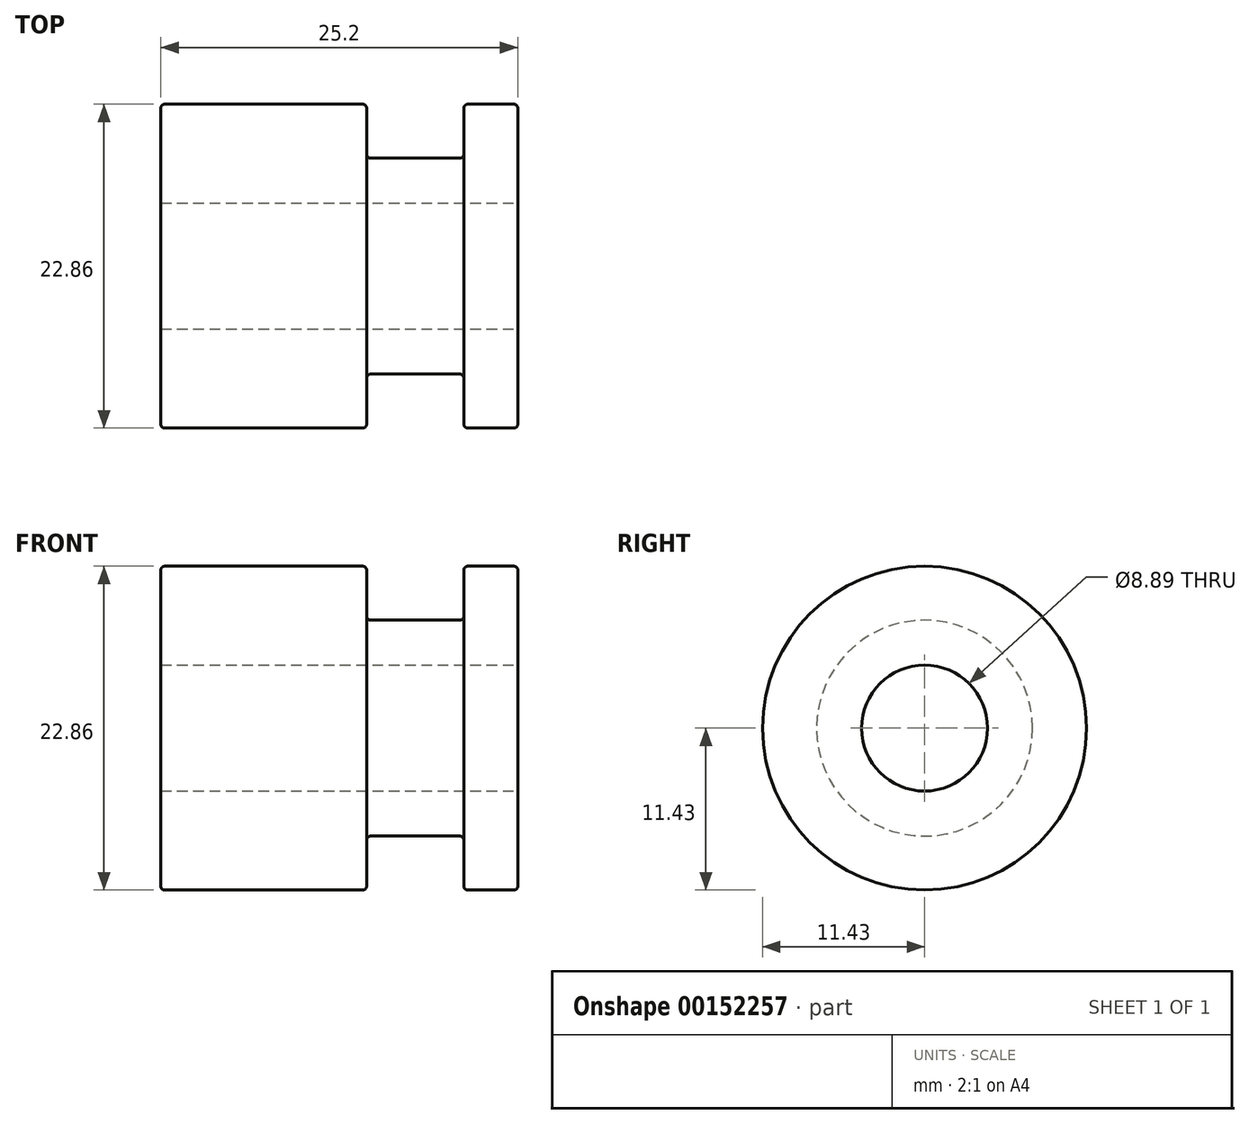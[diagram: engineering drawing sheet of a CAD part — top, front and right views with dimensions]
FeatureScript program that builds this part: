
annotation { "Feature Type Name" : "Feature", "Feature Type Description" : "" }
export const myFeature = defineFeature(function(context is Context, id is Id, definition is map)
    precondition{}
    {
        {
            var Q0;
            Q0=qCreatedBy(makeId("Front.planeOp"),FACE);
            var sketch = newSketch(context, id + "F0", { "sketchPlane" : qUnion([Q0])});
            skLineSegment(sketch, "E0", {"start": v(0, 0) * mm, "end": v(0, 11.15) * mm});
            skLineSegment(sketch, "E1", {"start": v(-0.28, 11.43) * mm, "end": v(-3.53, 11.43) * mm});
            skLineSegment(sketch, "E2", {"start": v(-3.8, 11.15) * mm, "end": v(-3.8, 7.9) * mm});
            skLineSegment(sketch, "E3", {"start": v(-4.1, 7.62) * mm, "end": v(-10.39, 7.62) * mm});
            skLineSegment(sketch, "E4", {"start": v(-10.67, 7.9) * mm, "end": v(-10.67, 11.15) * mm});
            skLineSegment(sketch, "E5", {"start": v(-10.95, 11.43) * mm, "end": v(-24.92, 11.43) * mm});
            skLineSegment(sketch, "E6", {"start": v(-25.2, 11.15) * mm, "end": v(-25.2, 7.62) * mm});
            skLineSegment(sketch, "E7", {"start": v(-25.2, 7.62) * mm, "end": v(-25.2, 0) * mm});
            skLineSegment(sketch, "E8", {"start": v(-25.2, 0) * mm, "end": v(0, 0) * mm});
            skPoint(sketch, "E9.visualSharp", {"position": v(-3.8, 7.62) * mm});
            skArc(sketch, "E9.filletArc", {"start": v(-4.1, 7.62) * mm, "mid": v(-3.9, 7.7) * mm, "end": v(-3.8, 7.9) * mm});
            skPoint(sketch, "E10.visualSharp", {"position": v(-10.67, 7.62) * mm});
            skArc(sketch, "E10.filletArc", {"start": v(-10.67, 7.9) * mm, "mid": v(-10.59, 7.7) * mm, "end": v(-10.39, 7.62) * mm});
            skPoint(sketch, "E11.visualSharp", {"position": v(-3.8, 11.43) * mm});
            skArc(sketch, "E11.filletArc", {"start": v(-3.53, 11.43) * mm, "mid": v(-3.73, 11.35) * mm, "end": v(-3.8, 11.15) * mm});
            skPoint(sketch, "E12.visualSharp", {"position": v(-10.67, 11.43) * mm});
            skArc(sketch, "E12.filletArc", {"start": v(-10.67, 11.15) * mm, "mid": v(-10.75, 11.35) * mm, "end": v(-10.95, 11.43) * mm});
            skPoint(sketch, "E13.visualSharp", {"position": v(-25.2, 11.43) * mm});
            skArc(sketch, "E13.filletArc", {"start": v(-24.92, 11.43) * mm, "mid": v(-25.12, 11.35) * mm, "end": v(-25.2, 11.15) * mm});
            skPoint(sketch, "E14.visualSharp", {"position": v(0, 11.43) * mm});
            skArc(sketch, "E14.filletArc", {"start": v(0, 11.15) * mm, "mid": v(-0.08, 11.35) * mm, "end": v(-0.28, 11.43) * mm});
            skSolve(sketch);
        }
        {
            var Q0;
            Q0 = qSketchRegion(id + "F0", true);
            var Q1;
            Q1=sQuery(id+"F0.wireOp",EDGE,"E8");
            revolve(context, id + "F1", {"entities" : qUnion([Q0]), "axis" : qUnion([Q1]), "revolveType" : RevolveType.FULL});
        }
        {
            var Q0;
            Q0=qCreatedBy(makeId("Right.planeOp"),FACE);
            var sketch = newSketch(context, id + "F2", { "sketchPlane" : qUnion([Q0])});
            skCircle(sketch, "E15", {"center": v(0, 0) * mm, "radius": 4.45 * mm});
            skSolve(sketch);
        }
        {
            var Q0;
            Q0 = qSketchRegion(id + "F2", true);
            extrude(context, id + "F3", {"entities" : qUnion([Q0]), "operationType" : NewBodyOperationType.REMOVE, "endBound" : BoundingType.THROUGH_ALL, "oppositeDirection" : true, "depth" : 25.4 * mm});
        }
    });
